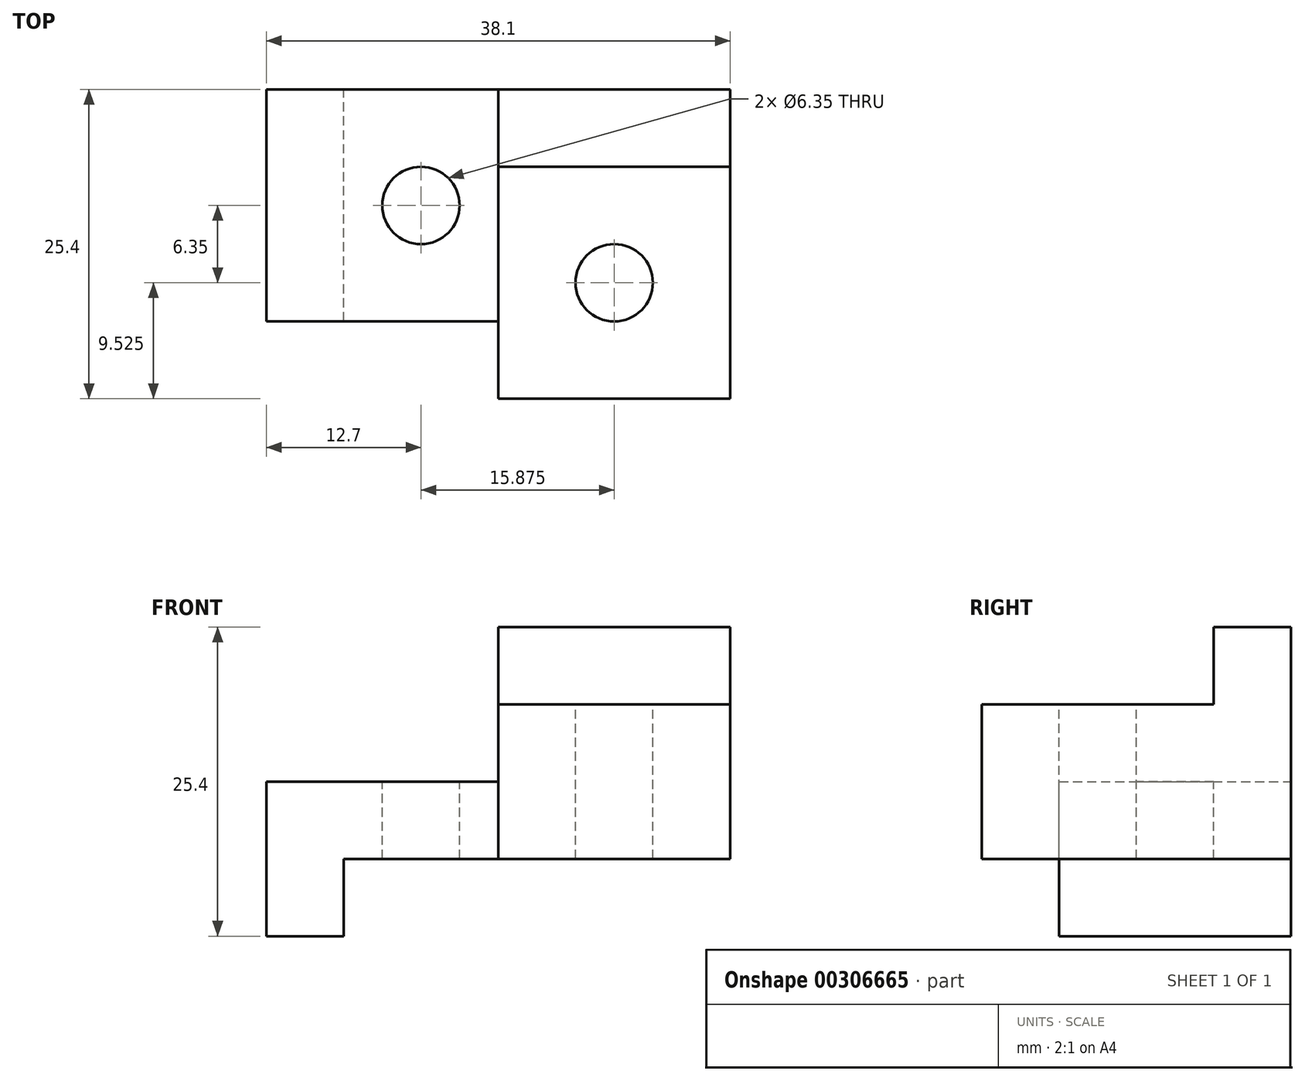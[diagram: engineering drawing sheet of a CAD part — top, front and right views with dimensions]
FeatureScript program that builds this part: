
annotation { "Feature Type Name" : "Feature", "Feature Type Description" : "" }
export const myFeature = defineFeature(function(context is Context, id is Id, definition is map)
    precondition{}
    {
        {
            var Q0;
            Q0=qCreatedBy(makeId("Front.planeOp"),FACE);
            var sketch = newSketch(context, id + "F0", { "sketchPlane" : qUnion([Q0])});
            skLineSegment(sketch, "E0", {"start": v(0, 0) * mm, "end": v(19.05, 0) * mm});
            skLineSegment(sketch, "E1", {"start": v(19.05, 0) * mm, "end": v(19.05, 6.35) * mm});
            skLineSegment(sketch, "E2", {"start": v(19.05, 6.35) * mm, "end": v(38.1, 6.35) * mm});
            skLineSegment(sketch, "E3", {"start": v(38.1, 6.35) * mm, "end": v(38.1, -6.35) * mm});
            skLineSegment(sketch, "E4", {"start": v(38.1, -6.35) * mm, "end": v(6.35, -6.35) * mm});
            skLineSegment(sketch, "E5", {"start": v(6.35, -6.35) * mm, "end": v(6.35, -12.7) * mm});
            skLineSegment(sketch, "E6", {"start": v(6.35, -12.7) * mm, "end": v(0, -12.7) * mm});
            skLineSegment(sketch, "E7", {"start": v(0, -12.7) * mm, "end": v(0, 0) * mm});
            skLineSegment(sketch, "E8", {"start": v(19.05, 6.35) * mm, "end": v(19.05, 12.7) * mm});
            skLineSegment(sketch, "E9", {"start": v(19.05, 12.7) * mm, "end": v(38.1, 12.7) * mm});
            skLineSegment(sketch, "E10", {"start": v(38.1, 12.7) * mm, "end": v(38.1, 6.35) * mm});
            skSolve(sketch);
        }
        {
            var Q0;
            Q0=makeQuery(id+"F0.imprint","IMPRINT",FACE,{"disambiguationData":[TD([[makeQuery(id+"F0.imprint","IMPRINT",EDGE,{"derivedFrom":sQuery(id+"F0.wireOp",EDGE,"E0")}),-1.0]])]});
            extrude(context, id + "F1", {"entities" : qUnion([Q0]), "depth" : 25.4 * mm});
        }
        {
            var Q0;
            Q0=makeQuery(id+"F0.imprint","IMPRINT",FACE,{"disambiguationData":[TD([[makeQuery(id+"F0.imprint","IMPRINT",EDGE,{"derivedFrom":sQuery(id+"F0.wireOp",EDGE,"E2")}),1.0]])]});
            extrude(context, id + "F2", {"entities" : qUnion([Q0]), "operationType" : NewBodyOperationType.ADD, "depth" : 6.35 * mm});
        }
        {
            var Q0;
            Q0=makeQuery(id+"F1.opExtrude","SWEPT_FACE",FACE,{"disambiguationData":[OSD([sQuery(id+"F0.wireOp",EDGE,"E2")])]});
            var sketch = newSketch(context, id + "F3", { "sketchPlane" : qUnion([Q0])});
            skLineSegment(sketch, "E11", {"start": v(38.1, -15.88) * mm, "end": v(19.05, -15.88) * mm, "construction": true});
            skCircle(sketch, "E12", {"center": v(28.58, -15.88) * mm, "radius": 3.18 * mm});
            skLineSegment(sketch, "E13", {"start": v(28.58, -6.35) * mm, "end": v(28.58, -25.4) * mm, "construction": true});
            skSolve(sketch);
        }
        {
            var Q0;
            Q0=makeQuery(id+"F3.imprint","IMPRINT",FACE,{"disambiguationData":[TD([[makeQuery(id+"F3.imprint","IMPRINT",EDGE,{"derivedFrom":sQuery(id+"F3.wireOp",EDGE,"E12")}),1.0]])]});
            extrude(context, id + "F4", {"entities" : qUnion([Q0]), "operationType" : NewBodyOperationType.REMOVE, "endBound" : BoundingType.THROUGH_ALL, "oppositeDirection" : true, "depth" : 25.4 * mm});
        }
        {
            var Q0;
            Q0=makeQuery(id+"F1.opExtrude","SWEPT_FACE",FACE,{"disambiguationData":[OSD([sQuery(id+"F0.wireOp",EDGE,"E0")])]});
            var sketch = newSketch(context, id + "F5", { "sketchPlane" : qUnion([Q0])});
            skLineSegment(sketch, "E14", {"start": v(0, -25.4) * mm, "end": v(0, -19.05) * mm});
            skLineSegment(sketch, "E15", {"start": v(0, -19.05) * mm, "end": v(19.05, -19.05) * mm});
            skLineSegment(sketch, "E16", {"start": v(19.05, -19.05) * mm, "end": v(19.05, -25.4) * mm});
            skLineSegment(sketch, "E17", {"start": v(19.05, -25.4) * mm, "end": v(0, -25.4) * mm});
            skSolve(sketch);
        }
        {
            var Q0;
            Q0=makeQuery(id+"F5.imprint","IMPRINT",FACE,{"disambiguationData":[TD([[makeQuery(id+"F5.imprint","IMPRINT",EDGE,{"derivedFrom":sQuery(id+"F5.wireOp",EDGE,"E14")}),-1.0]])]});
            extrude(context, id + "F6", {"entities" : qUnion([Q0]), "operationType" : NewBodyOperationType.REMOVE, "endBound" : BoundingType.THROUGH_ALL, "oppositeDirection" : true, "depth" : 25.4 * mm});
        }
        {
            var Q0;
            Q0=makeQuery(id+"F1.opExtrude","SWEPT_FACE",FACE,{"disambiguationData":[OSD([sQuery(id+"F0.wireOp",EDGE,"E0")])]});
            var sketch = newSketch(context, id + "F7", { "sketchPlane" : qUnion([Q0])});
            skCircle(sketch, "E18", {"center": v(12.7, -9.53) * mm, "radius": 3.18 * mm});
            skLineSegment(sketch, "E19", {"start": v(0, -9.53) * mm, "end": v(21, -9.53) * mm, "construction": true});
            skPoint(sketch, "E19.endSnap0", {"position": v(19.05, -9.53) * mm});
            skSolve(sketch);
        }
        {
            var Q0;
            Q0=makeQuery(id+"F7.imprint","IMPRINT",FACE,{"disambiguationData":[TD([[makeQuery(id+"F7.imprint","IMPRINT",EDGE,{"derivedFrom":sQuery(id+"F7.wireOp",EDGE,"E18")}),1.0]])]});
            extrude(context, id + "F8", {"entities" : qUnion([Q0]), "operationType" : NewBodyOperationType.REMOVE, "endBound" : BoundingType.THROUGH_ALL, "oppositeDirection" : true, "depth" : 25.4 * mm});
        }
    });
